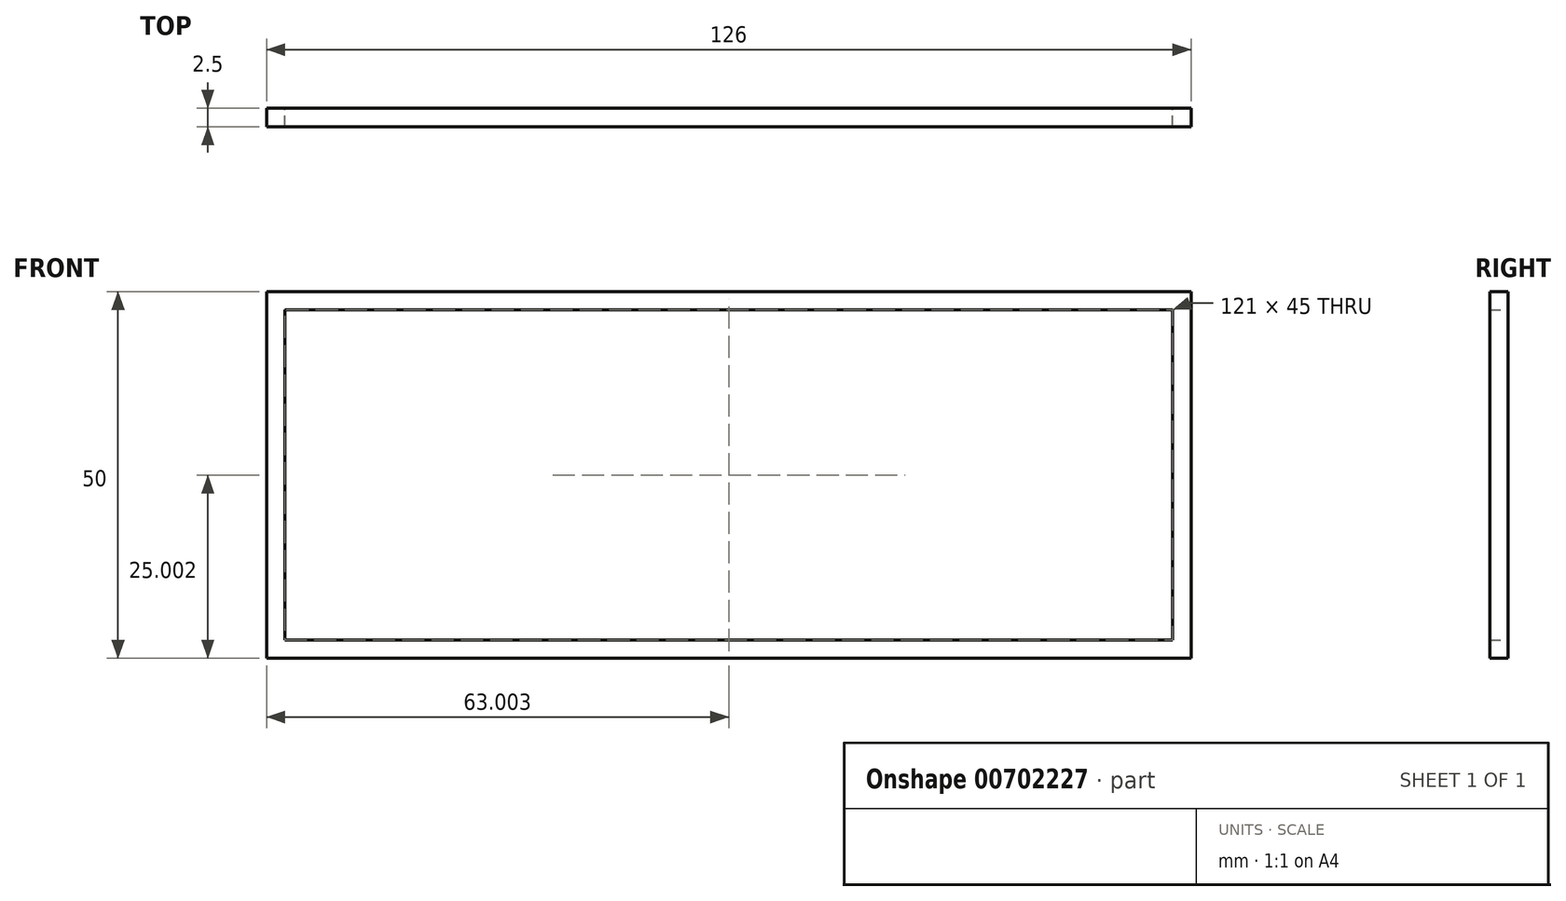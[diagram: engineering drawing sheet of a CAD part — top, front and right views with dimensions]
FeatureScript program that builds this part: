
annotation { "Feature Type Name" : "Feature", "Feature Type Description" : "" }
export const myFeature = defineFeature(function(context is Context, id is Id, definition is map)
    precondition{}
    {
        {
            var Q0;
            Q0=qCreatedBy(makeId("Front.planeOp"),FACE);
            var sketch = newSketch(context, id + "F0", { "sketchPlane" : qUnion([Q0])});
            skLineSegment(sketch, "E0.bottom", {"start": v(-45.34, -21.29) * mm, "end": v(80.66, -21.29) * mm});
            skLineSegment(sketch, "E0.top", {"start": v(-45.34, 28.71) * mm, "end": v(80.66, 28.71) * mm});
            skLineSegment(sketch, "E0.left", {"start": v(-45.34, -21.29) * mm, "end": v(-45.34, 28.71) * mm});
            skLineSegment(sketch, "E0.right", {"start": v(80.66, -21.29) * mm, "end": v(80.66, 28.71) * mm});
            skLineSegment(sketch, "E1.bottom", {"start": v(-42.84, -18.79) * mm, "end": v(78.16, -18.79) * mm});
            skLineSegment(sketch, "E1.top", {"start": v(-42.84, 26.21) * mm, "end": v(78.16, 26.21) * mm});
            skLineSegment(sketch, "E1.left", {"start": v(-42.84, -18.79) * mm, "end": v(-42.84, 26.21) * mm});
            skLineSegment(sketch, "E1.right", {"start": v(78.16, -18.79) * mm, "end": v(78.16, 26.21) * mm});
            skSolve(sketch);
        }
        {
            var Q0;
            Q0=makeQuery(id+"F0.imprint","IMPRINT",FACE,{"disambiguationData":[TD([[makeQuery(id+"F0.imprint","IMPRINT",EDGE,{"derivedFrom":sQuery(id+"F0.wireOp",EDGE,"E0.bottom")}),1.0]])]});
            extrude(context, id + "F1", {"entities" : qUnion([Q0]), "depth" : 2.5 * mm, "offsetDistance" : 25 * mm});
        }
    });
